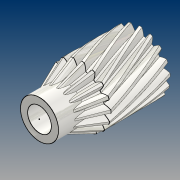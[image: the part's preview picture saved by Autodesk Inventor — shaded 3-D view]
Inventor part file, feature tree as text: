
AUTODESK INVENTOR PART (.ipt)
format: ipt  version: 2021 (Build 250183000, 183)  size: 1,044,480 bytes
history: native  units: mm (DEFAULTED — no unit token found)
features: sketch x7, extrude x6, plane x6, other x5, projected_geometry x4, loft x1, pattern_circular x1, mirror x1
ambient origin geometry x8: Origin, YZ Plane, XZ Plane, XY Plane, X Axis, Y Axis, Z Axis, Center Point
bodies: Solid1 (feature_tree)
feature tree (31):
  extrude  "Extrusion1"  Depth=25.0mm TaperAngle=0.0deg
  plane  "Work Plane2"
  plane  "Work Plane8"
  plane  "Work Plane9"
  other  "Spur Gear"
  sketch  "Sketch3"  dims[d16=40.0mm d17=0.0mm d34=1.847996mm]
  extrude  "Extrusion2"  Depth=10.0mm TaperAngle=0.0deg
  extrude  "Extrusion3"  Depth=1.847996mm TaperAngle=0.0deg
  plane  "Work Plane11"
  sketch  "Sketch4"  dims[d39=0.0mm d41=0.0mm]
  plane  "Work Plane12"
  sketch  "Sketch6"  dims[d43=40.0mm d46=40.0mm]
  sketch  "Sketch9"  dims[d47=0.0mm d48=0.0mm d49=10.0mm]
  sketch  "Sketch10"  dims[d51=10.0mm d52=0.0mm d53=17.5mm d54=0.0mm d55=3.5mm d64=4.0mm d65=2.0mm d66=2.5mm d67=0.0mm d68=7.75mm d69=0.0mm d70=6.5mm d71=0.0mm d72=20.0mm d73=90.0deg d75=3.0mm d76=0.0mm d77=90.0deg d78=0.0mm d79=90.0deg]
  loft  "Loft2"
  extrude  "Extrusion4"  Depth=40.0mm
  extrude  "Extrusion5"  Depth=10.0mm
  extrude  "Extrusion6"  Depth=17.5mm TaperAngle=0.0deg
  pattern_circular  "Circular Pattern1"  [2 undecoded]
  plane  "Work Plane13"
  mirror  "Mirror1"
  sketch  "Sketch1"  dims[d0=25.112479mm d1=25.0mm d2=0.0mm]
  sketch  "Sketch2"  dims[d3=22.613778mm d4=10.0mm d5=0.0mm]
  other  "Srf1"
  projected_geometry  "Projected Loop1"
  projected_geometry  "Projected Loop3"
  projected_geometry  "Projected Loop19"
  projected_geometry  "Projected Loop20"
  other  "Edges3"
  other  "Edges4"
  other  "Pitch Diameter"
note: 2 required parameter values undecoded (feature->parameter linkage not recoverable at this tier; creation-order binding heuristic only, values carry confidence <= 0.55)
